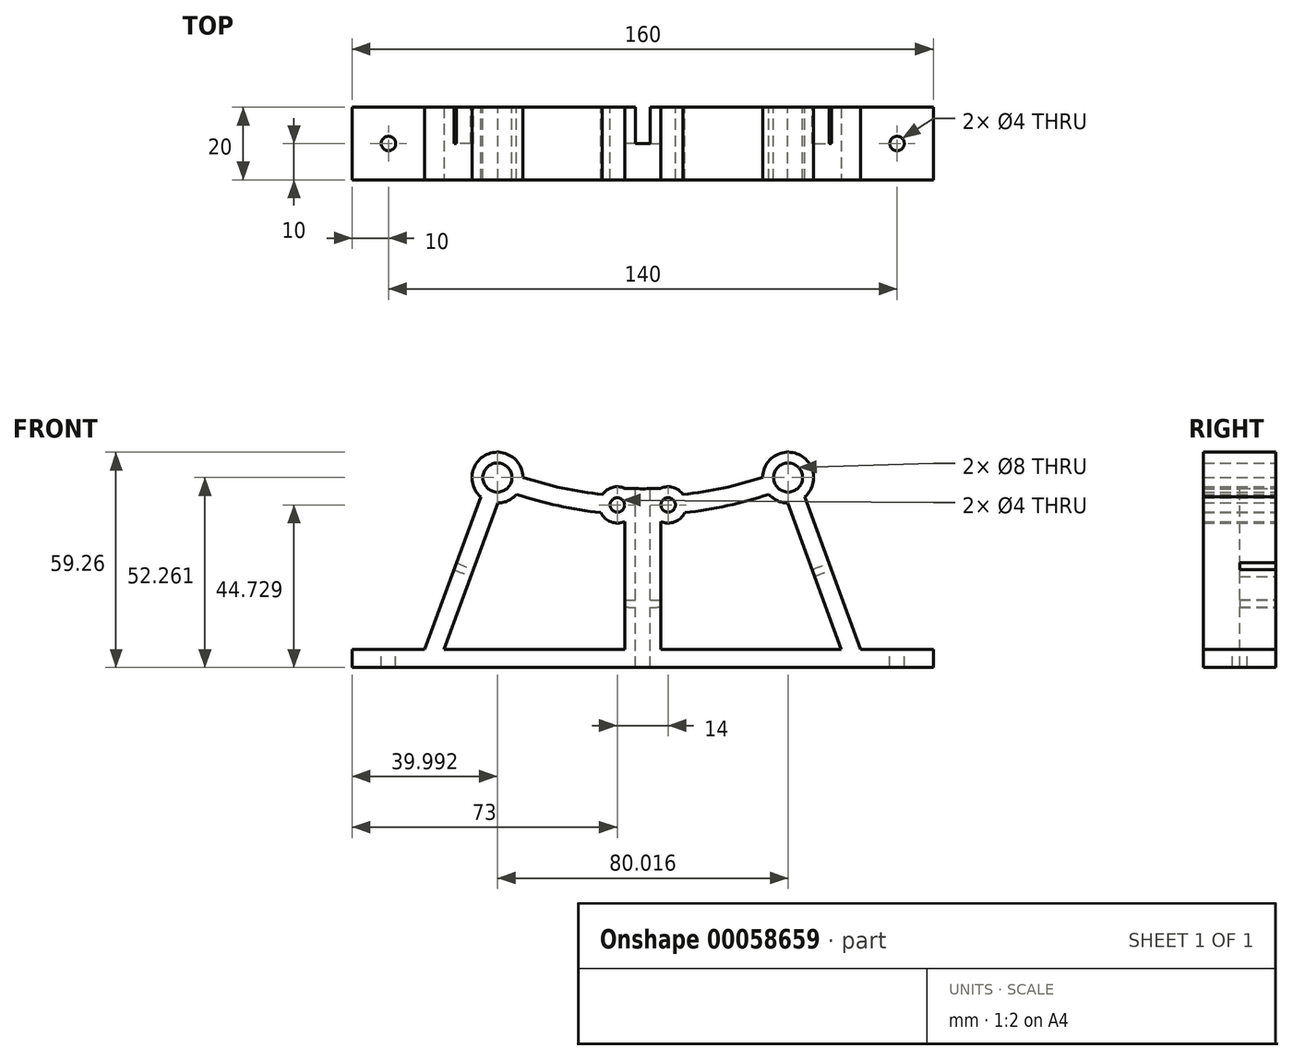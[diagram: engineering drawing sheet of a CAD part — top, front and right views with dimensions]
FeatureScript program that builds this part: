
annotation { "Feature Type Name" : "Feature", "Feature Type Description" : "" }
export const myFeature = defineFeature(function(context is Context, id is Id, definition is map)
    precondition{}
    {
        {
            var Q0;
            Q0=qCreatedBy(makeId("Front.planeOp"),FACE);
            var sketch = newSketch(context, id + "F0", { "sketchPlane" : qUnion([Q0])});
            skLineSegment(sketch, "E0", {"start": v(0, 0) * mm, "end": v(80, 0) * mm});
            skLineSegment(sketch, "E1", {"start": v(80, 0) * mm, "end": v(80, 5) * mm});
            skLineSegment(sketch, "E2", {"start": v(80, 5) * mm, "end": v(60, 5) * mm});
            skLineSegment(sketch, "E3", {"start": v(60, 5) * mm, "end": v(10.5, 140) * mm});
            skLineSegment(sketch, "E4", {"start": v(0, 0) * mm, "end": v(0, 151.5) * mm, "construction": true});
            skLineSegment(sketch, "E5.rect.bottom", {"start": v(21, 140) * mm, "end": v(0, 140) * mm, "construction": true});
            skLineSegment(sketch, "E5.rect.left", {"start": v(21, 140) * mm, "end": v(21, 163) * mm});
            skCircle(sketch, "E6", {"center": v(0, 151.5) * mm, "radius": 135 * mm, "construction": true});
            skCircle(sketch, "E7", {"center": v(0, 151.5) * mm, "radius": 133 * mm, "construction": true});
            skCircle(sketch, "E8", {"center": v(0, 151.5) * mm, "radius": 100 * mm, "construction": true});
            skLineSegment(sketch, "E9", {"start": v(21, 163) * mm, "end": v(0, 163) * mm, "construction": true});
            skLineSegment(sketch, "E10", {"start": v(0, 163) * mm, "end": v(0, 151.5) * mm, "construction": true});
            skLineSegment(sketch, "E11", {"start": v(35.25, 72.5) * mm, "end": v(0, 72.5) * mm});
            skLineSegment(sketch, "E12", {"start": v(0, 151.5) * mm, "end": v(21, 151.5) * mm, "construction": true});
            skSolve(sketch);
        }
        {
            var Q0;
            Q0=qCreatedBy(makeId("Front.planeOp"),FACE);
            var sketch = newSketch(context, id + "F1", { "sketchPlane" : qUnion([Q0])});
            skLineSegment(sketch, "E13.bottom", {"start": v(0, 0) * mm, "end": v(80, 0) * mm});
            skLineSegment(sketch, "E13.top", {"start": v(0, 5) * mm, "end": v(80, 5) * mm});
            skLineSegment(sketch, "E13.left", {"start": v(0, 0) * mm, "end": v(0, 5) * mm});
            skLineSegment(sketch, "E13.right", {"start": v(80, 0) * mm, "end": v(80, 5) * mm});
            skSolve(sketch);
        }
        {
            var Q0;
            Q0 = qSketchRegion(id + "F1", true);
            extrude(context, id + "F2", {"entities" : qUnion([Q0]), "depth" : 10 * mm});
        }
        {
            var Q0;
            Q0=qCreatedBy(makeId("Front.planeOp"),FACE);
            var sketch = newSketch(context, id + "F3", { "sketchPlane" : qUnion([Q0])});
            skLineSegment(sketch, "E14", {"start": v(0, 0) * mm, "end": v(0, 151.5) * mm});
            skLineSegment(sketch, "E15", {"start": v(0, 151.5) * mm, "end": v(5, 151.5) * mm});
            skLineSegment(sketch, "E16", {"start": v(5, 151.5) * mm, "end": v(5, 0) * mm});
            skLineSegment(sketch, "E17", {"start": v(5, 0) * mm, "end": v(0, 0) * mm});
            skSolve(sketch);
        }
        {
            var Q0;
            Q0 = qSketchRegion(id + "F3", true);
            var Q1;
            Q1=makeQuery(id+"F2.opExtrude","CAP_FACE",FACE,{"disambiguationData":[OSD([sQuery(id+"F1.wireOp",EDGE,"E13.bottom"),sQuery(id+"F1.wireOp",EDGE,"E13.top"),sQuery(id+"F1.wireOp",EDGE,"E13.left"),sQuery(id+"F1.wireOp",EDGE,"E13.right")])],"isStart":false});
            extrude(context, id + "F4", {"entities" : qUnion([Q0]), "operationType" : NewBodyOperationType.ADD, "endBound" : BoundingType.UP_TO_SURFACE, "endBoundEntityFace" : qUnion([Q1]), "depth" : 25 * mm});
        }
        {
            var Q0;
            Q0=qCreatedBy(makeId("Front.planeOp"),FACE);
            var sketch = newSketch(context, id + "F5", { "sketchPlane" : qUnion([Q0])});
            skLineSegment(sketch, "E18.bottom", {"start": v(0, 163) * mm, "end": v(21, 163) * mm});
            skLineSegment(sketch, "E18.top", {"start": v(0, 140) * mm, "end": v(21, 140) * mm});
            skLineSegment(sketch, "E18.left", {"start": v(0, 163) * mm, "end": v(0, 140) * mm});
            skLineSegment(sketch, "E18.right", {"start": v(21, 163) * mm, "end": v(21, 140) * mm});
            skSolve(sketch);
        }
        {
            var Q0;
            Q0 = qSketchRegion(id + "F5", true);
            var Q1;
            Q1=makeQuery(id+"F4.boolean.opBoolean","MERGE",FACE,{"derivedFrom":[makeQuery(id+"F2.opExtrude","CAP_FACE",FACE,{"disambiguationData":[OSD([sQuery(id+"F1.wireOp",EDGE,"E13.bottom"),sQuery(id+"F1.wireOp",EDGE,"E13.top"),sQuery(id+"F1.wireOp",EDGE,"E13.left"),sQuery(id+"F1.wireOp",EDGE,"E13.right")])],"isStart":false}),makeQuery(id+"F4.opExtrude","CAP_FACE",FACE,{"disambiguationData":[OSD([sQuery(id+"F3.wireOp",EDGE,"E14"),sQuery(id+"F3.wireOp",EDGE,"E15"),sQuery(id+"F3.wireOp",EDGE,"E16"),sQuery(id+"F3.wireOp",EDGE,"E17")])],"isStart":false})]});
            extrude(context, id + "F6", {"entities" : qUnion([Q0]), "operationType" : NewBodyOperationType.ADD, "endBound" : BoundingType.UP_TO_SURFACE, "endBoundEntityFace" : qUnion([Q1]), "depth" : 25 * mm});
        }
        {
            var Q0;
            Q0=qCreatedBy(makeId("Front.planeOp"),FACE);
            var sketch = newSketch(context, id + "F7", { "sketchPlane" : qUnion([Q0])});
            skLineSegment(sketch, "E19", {"start": v(9.87, 141.72) * mm, "end": v(60, 5) * mm});
            skLineSegment(sketch, "E20", {"start": v(60, 5) * mm, "end": v(55.3, 3.28) * mm});
            skLineSegment(sketch, "E21", {"start": v(55.3, 3.28) * mm, "end": v(5.17, 140) * mm});
            skLineSegment(sketch, "E22", {"start": v(5.17, 140) * mm, "end": v(9.87, 141.72) * mm});
            skSolve(sketch);
        }
        {
            var Q0;
            Q0 = qSketchRegion(id + "F7", true);
            var Q1;
            Q1=makeQuery(id+"F6.boolean.opBoolean","MERGE",FACE,{"derivedFrom":[makeQuery(id+"F4.boolean.opBoolean","MERGE",FACE,{"derivedFrom":[makeQuery(id+"F2.opExtrude","CAP_FACE",FACE,{"disambiguationData":[OSD([sQuery(id+"F1.wireOp",EDGE,"E13.bottom"),sQuery(id+"F1.wireOp",EDGE,"E13.top"),sQuery(id+"F1.wireOp",EDGE,"E13.left"),sQuery(id+"F1.wireOp",EDGE,"E13.right")])],"isStart":false}),makeQuery(id+"F4.opExtrude","CAP_FACE",FACE,{"disambiguationData":[OSD([sQuery(id+"F3.wireOp",EDGE,"E14"),sQuery(id+"F3.wireOp",EDGE,"E15"),sQuery(id+"F3.wireOp",EDGE,"E16"),sQuery(id+"F3.wireOp",EDGE,"E17")])],"isStart":false})]}),makeQuery(id+"F6.opExtrude","CAP_FACE",FACE,{"disambiguationData":[OSD([sQuery(id+"F5.wireOp",EDGE,"E18.bottom"),sQuery(id+"F5.wireOp",EDGE,"E18.top"),sQuery(id+"F5.wireOp",EDGE,"E18.left"),sQuery(id+"F5.wireOp",EDGE,"E18.right")])],"isStart":false})]});
            extrude(context, id + "F8", {"entities" : qUnion([Q0]), "operationType" : NewBodyOperationType.ADD, "endBound" : BoundingType.UP_TO_SURFACE, "endBoundEntityFace" : qUnion([Q1]), "depth" : 25 * mm});
        }
        {
            var Q0;
            Q0=makeQuery(id+"F8.boolean.opBoolean","MERGE",FACE,{"derivedFrom":[makeQuery(id+"F6.boolean.opBoolean","MERGE",FACE,{"derivedFrom":[makeQuery(id+"F4.boolean.opBoolean","MERGE",FACE,{"derivedFrom":[makeQuery(id+"F2.opExtrude","CAP_FACE",FACE,{"disambiguationData":[OSD([sQuery(id+"F1.wireOp",EDGE,"E13.bottom"),sQuery(id+"F1.wireOp",EDGE,"E13.top"),sQuery(id+"F1.wireOp",EDGE,"E13.left"),sQuery(id+"F1.wireOp",EDGE,"E13.right")])],"isStart":false}),makeQuery(id+"F4.opExtrude","CAP_FACE",FACE,{"disambiguationData":[OSD([sQuery(id+"F3.wireOp",EDGE,"E14"),sQuery(id+"F3.wireOp",EDGE,"E15"),sQuery(id+"F3.wireOp",EDGE,"E16"),sQuery(id+"F3.wireOp",EDGE,"E17")])],"isStart":false})]}),makeQuery(id+"F6.opExtrude","CAP_FACE",FACE,{"disambiguationData":[OSD([sQuery(id+"F5.wireOp",EDGE,"E18.bottom"),sQuery(id+"F5.wireOp",EDGE,"E18.top"),sQuery(id+"F5.wireOp",EDGE,"E18.left"),sQuery(id+"F5.wireOp",EDGE,"E18.right")])],"isStart":false})]}),makeQuery(id+"F8.opExtrude","CAP_FACE",FACE,{"disambiguationData":[OSD([sQuery(id+"F7.wireOp",EDGE,"E19"),sQuery(id+"F7.wireOp",EDGE,"E20"),sQuery(id+"F7.wireOp",EDGE,"E21"),sQuery(id+"F7.wireOp",EDGE,"E22")])],"isStart":false})]});
            var sketch = newSketch(context, id + "F9", { "sketchPlane" : qUnion([Q0])});
            skLineSegment(sketch, "E23.0", {"start": v(54.67, 5) * mm, "end": v(5.17, 140) * mm});
            skLineSegment(sketch, "E24.0", {"start": v(5, 140) * mm, "end": v(5, 5) * mm});
            skLineSegment(sketch, "E25.0", {"start": v(5, 5) * mm, "end": v(54.67, 5) * mm});
            skLineSegment(sketch, "E26.0", {"start": v(0, 0) * mm, "end": v(0, 163) * mm});
            skLineSegment(sketch, "E27.0", {"start": v(0, 0) * mm, "end": v(80, 0) * mm});
            skLineSegment(sketch, "E28.0", {"start": v(60, 5) * mm, "end": v(80, 5) * mm});
            skLineSegment(sketch, "E28.1", {"start": v(80, 0) * mm, "end": v(80, 5) * mm});
            skLineSegment(sketch, "E28.2", {"start": v(10.5, 140) * mm, "end": v(60, 5) * mm});
            skLineSegment(sketch, "E29.0", {"start": v(10.5, 140) * mm, "end": v(21, 140) * mm});
            skLineSegment(sketch, "E29.1", {"start": v(21, 163) * mm, "end": v(21, 140) * mm});
            skLineSegment(sketch, "E29.2", {"start": v(0, 163) * mm, "end": v(21, 163) * mm});
            skSolve(sketch);
        }
        {
            var Q0;
            Q0=makeQuery(id+"F9.imprint","IMPRINT",FACE,{"disambiguationData":[TD([[makeQuery(id+"F9.imprint","IMPRINT",EDGE,{"derivedFrom":sQuery(id+"F9.wireOp",EDGE,"E23.0")}),-1.0]])]});
            extrude(context, id + "F10", {"entities" : qUnion([Q0]), "operationType" : NewBodyOperationType.ADD, "depth" : 10 * mm});
        }
        {
            var Q0;
            Q0=makeQuery(id+"F8.boolean.opBoolean","MERGE",FACE,{"derivedFrom":[makeQuery(id+"F6.boolean.opBoolean","MERGE",FACE,{"derivedFrom":[makeQuery(id+"F4.boolean.opBoolean","MERGE",FACE,{"derivedFrom":[makeQuery(id+"F2.opExtrude","CAP_FACE",FACE,{"disambiguationData":[OSD([sQuery(id+"F1.wireOp",EDGE,"E13.bottom"),sQuery(id+"F1.wireOp",EDGE,"E13.top"),sQuery(id+"F1.wireOp",EDGE,"E13.left"),sQuery(id+"F1.wireOp",EDGE,"E13.right")])],"isStart":true}),makeQuery(id+"F4.opExtrude","CAP_FACE",FACE,{"disambiguationData":[OSD([sQuery(id+"F3.wireOp",EDGE,"E14"),sQuery(id+"F3.wireOp",EDGE,"E15"),sQuery(id+"F3.wireOp",EDGE,"E16"),sQuery(id+"F3.wireOp",EDGE,"E17")])],"isStart":true})]}),makeQuery(id+"F6.opExtrude","CAP_FACE",FACE,{"disambiguationData":[OSD([sQuery(id+"F5.wireOp",EDGE,"E18.bottom"),sQuery(id+"F5.wireOp",EDGE,"E18.top"),sQuery(id+"F5.wireOp",EDGE,"E18.left"),sQuery(id+"F5.wireOp",EDGE,"E18.right")])],"isStart":true})]}),makeQuery(id+"F8.opExtrude","CAP_FACE",FACE,{"disambiguationData":[OSD([sQuery(id+"F7.wireOp",EDGE,"E19"),sQuery(id+"F7.wireOp",EDGE,"E20"),sQuery(id+"F7.wireOp",EDGE,"E21"),sQuery(id+"F7.wireOp",EDGE,"E22")])],"isStart":true})]});
            var sketch = newSketch(context, id + "F11", { "sketchPlane" : qUnion([Q0])});
            skLineSegment(sketch, "E30", {"start": v(0, 0) * mm, "end": v(-2, 0) * mm});
            skLineSegment(sketch, "E31", {"start": v(-2, 0) * mm, "end": v(-2, 138) * mm});
            skLineSegment(sketch, "E32", {"start": v(-2, 138) * mm, "end": v(-21, 138) * mm});
            skLineSegment(sketch, "E33", {"start": v(-21, 138) * mm, "end": v(-21, 140) * mm});
            skLineSegment(sketch, "E34", {"start": v(-21, 140) * mm, "end": v(0, 140) * mm});
            skLineSegment(sketch, "E35", {"start": v(0, 140) * mm, "end": v(0, 0) * mm});
            skSolve(sketch);
        }
        {
            var Q0;
            Q0 = qSketchRegion(id + "F11", true);
            extrude(context, id + "F12", {"entities" : qUnion([Q0]), "operationType" : NewBodyOperationType.REMOVE, "oppositeDirection" : true, "depth" : 10 * mm});
        }
        {
            var Q0;
            {var subQ0=sQuery(id+"F7.wireOp",EDGE,"E21");var subQ1=sQuery(id+"F7.wireOp",EDGE,"E19");var subQ2=sQuery(id+"F1.wireOp",EDGE,"E13.bottom");var subQ3=sQuery(id+"F1.wireOp",EDGE,"E13.top");var subQ4=sQuery(id+"F1.wireOp",EDGE,"E13.right");var subQ5=sQuery(id+"F3.wireOp",EDGE,"E16");Q0=makeQuery(id+"F12.boolean.opBoolean","SPLIT",FACE,{"disambiguationData":[TD([makeQuery(id+"F2.opExtrude","SWEPT_FACE",FACE,{"disambiguationData":[OSD([subQ2])]})])],"derivedFrom":makeQuery(id+"F8.boolean.opBoolean","MERGE",FACE,{"derivedFrom":[makeQuery(id+"F6.boolean.opBoolean","MERGE",FACE,{"derivedFrom":[makeQuery(id+"F4.boolean.opBoolean","MERGE",FACE,{"derivedFrom":[makeQuery(id+"F2.opExtrude","CAP_FACE",FACE,{"disambiguationData":[OSD([subQ2,subQ3,sQuery(id+"F1.wireOp",EDGE,"E13.left"),subQ4])],"isStart":true}),makeQuery(id+"F4.opExtrude","CAP_FACE",FACE,{"disambiguationData":[OSD([sQuery(id+"F3.wireOp",EDGE,"E14"),sQuery(id+"F3.wireOp",EDGE,"E15"),subQ5,sQuery(id+"F3.wireOp",EDGE,"E17")])],"isStart":true})]}),makeQuery(id+"F6.opExtrude","CAP_FACE",FACE,{"disambiguationData":[OSD([sQuery(id+"F5.wireOp",EDGE,"E18.bottom"),sQuery(id+"F5.wireOp",EDGE,"E18.top"),sQuery(id+"F5.wireOp",EDGE,"E18.left"),sQuery(id+"F5.wireOp",EDGE,"E18.right")])],"isStart":true})]}),makeQuery(id+"F8.opExtrude","CAP_FACE",FACE,{"disambiguationData":[OSD([subQ1,sQuery(id+"F7.wireOp",EDGE,"E20"),subQ0,sQuery(id+"F7.wireOp",EDGE,"E22")])],"isStart":true})]})});}
            var sketch = newSketch(context, id + "F13", { "sketchPlane" : qUnion([Q0])});
            skLineSegment(sketch, "E36", {"start": v(-2, 138) * mm, "end": v(-11.23, 138) * mm});
            skLineSegment(sketch, "E37", {"start": v(-11.23, 138) * mm, "end": v(-13.07, 133) * mm});
            skLineSegment(sketch, "E38", {"start": v(-13.07, 133) * mm, "end": v(-2, 133) * mm});
            skLineSegment(sketch, "E39", {"start": v(-2, 133) * mm, "end": v(-2, 138) * mm});
            skSolve(sketch);
        }
        {
            var Q0;
            Q0 = qSketchRegion(id + "F13", true);
            extrude(context, id + "F14", {"entities" : qUnion([Q0]), "operationType" : NewBodyOperationType.ADD, "oppositeDirection" : true, "depth" : 20 * mm});
        }
        {
            var Q0;
            Q0=makeQuery(id+"F14.boolean.opBoolean","MERGE",FACE,{"derivedFrom":[makeQuery(id+"F10.opExtrude","CAP_FACE",FACE,{"disambiguationData":[OSD([sQuery(id+"F5.wireOp",EDGE,"E18.top"),sQuery(id+"F9.wireOp",EDGE,"E23.0"),sQuery(id+"F9.wireOp",EDGE,"E24.0"),sQuery(id+"F9.wireOp",EDGE,"E25.0"),sQuery(id+"F9.wireOp",EDGE,"E26.0"),sQuery(id+"F9.wireOp",EDGE,"E27.0"),sQuery(id+"F9.wireOp",EDGE,"E28.0"),sQuery(id+"F9.wireOp",EDGE,"E28.1"),sQuery(id+"F9.wireOp",EDGE,"E28.2"),sQuery(id+"F9.wireOp",EDGE,"E29.0"),sQuery(id+"F9.wireOp",EDGE,"E29.1"),sQuery(id+"F9.wireOp",EDGE,"E29.2")])],"isStart":false}),makeQuery(id+"F14.opExtrude","CAP_FACE",FACE,{"disambiguationData":[OSD([sQuery(id+"F13.wireOp",EDGE,"E36"),sQuery(id+"F13.wireOp",EDGE,"E37"),sQuery(id+"F13.wireOp",EDGE,"E38"),sQuery(id+"F13.wireOp",EDGE,"E39")])],"isStart":false})]});
            var sketch = newSketch(context, id + "F15", { "sketchPlane" : qUnion([Q0])});
            skLineSegment(sketch, "E40.bottom", {"start": v(5, 140) * mm, "end": v(5.9, 140) * mm});
            skLineSegment(sketch, "E40.top", {"start": v(5, 138) * mm, "end": v(5.9, 138) * mm});
            skLineSegment(sketch, "E40.left", {"start": v(5, 140) * mm, "end": v(5, 138) * mm});
            skLineSegment(sketch, "E40.right", {"start": v(5.9, 140) * mm, "end": v(5.9, 138) * mm});
            skSolve(sketch);
        }
        {
            var Q0;
            Q0 = qSketchRegion(id + "F15", true);
            extrude(context, id + "F16", {"entities" : qUnion([Q0]), "operationType" : NewBodyOperationType.ADD, "oppositeDirection" : true, "depth" : 10 * mm});
        }
        {
            var Q0;
            Q0=qCreatedBy(makeId("Front.planeOp"),FACE);
            var sketch = newSketch(context, id + "F17", { "sketchPlane" : qUnion([Q0])});
            skCircle(sketch, "E41.0", {"center": v(0, 151.5) * mm, "radius": 135 * mm});
            skCircle(sketch, "E41.1", {"center": v(0, 151.5) * mm, "radius": 133 * mm});
            skSolve(sketch);
        }
        {
            var Q0;
            Q0 = qSketchRegion(id + "F17", true);
            extrude(context, id + "F18", {"entities" : qUnion([Q0]), "operationType" : NewBodyOperationType.REMOVE, "depth" : 10 * mm});
        }
        {
            var Q0;
            Q0=qCreatedBy(makeId("Front.planeOp"),FACE);
            var sketch = newSketch(context, id + "F19", { "sketchPlane" : qUnion([Q0])});
            skCircle(sketch, "E42", {"center": v(40, 52.26) * mm, "radius": 7 * mm});
            skCircle(sketch, "E43", {"center": v(40, 52.26) * mm, "radius": 4 * mm});
            skPoint(sketch, "E44", {"position": v(42.36, 53.12) * mm});
            skPoint(sketch, "E45", {"position": v(37.66, 51.4) * mm});
            skLineSegment(sketch, "E46", {"start": v(37.66, 51.4) * mm, "end": v(42.36, 53.12) * mm, "construction": true});
            skSolve(sketch);
        }
        {
            var Q0;
            Q0 = qSketchRegion(id + "F19", true);
            var Q1;
            Q1=makeQuery(id+"F16.boolean.opBoolean","MERGE",FACE,{"derivedFrom":[makeQuery(id+"F14.boolean.opBoolean","MERGE",FACE,{"derivedFrom":[makeQuery(id+"F10.opExtrude","CAP_FACE",FACE,{"disambiguationData":[OSD([sQuery(id+"F5.wireOp",EDGE,"E18.top"),sQuery(id+"F9.wireOp",EDGE,"E23.0"),sQuery(id+"F9.wireOp",EDGE,"E24.0"),sQuery(id+"F9.wireOp",EDGE,"E25.0"),sQuery(id+"F9.wireOp",EDGE,"E26.0"),sQuery(id+"F9.wireOp",EDGE,"E27.0"),sQuery(id+"F9.wireOp",EDGE,"E28.0"),sQuery(id+"F9.wireOp",EDGE,"E28.1"),sQuery(id+"F9.wireOp",EDGE,"E28.2"),sQuery(id+"F9.wireOp",EDGE,"E29.0"),sQuery(id+"F9.wireOp",EDGE,"E29.1"),sQuery(id+"F9.wireOp",EDGE,"E29.2")])],"isStart":false}),makeQuery(id+"F14.opExtrude","CAP_FACE",FACE,{"disambiguationData":[OSD([sQuery(id+"F13.wireOp",EDGE,"E36"),sQuery(id+"F13.wireOp",EDGE,"E37"),sQuery(id+"F13.wireOp",EDGE,"E38"),sQuery(id+"F13.wireOp",EDGE,"E39")])],"isStart":false})]}),makeQuery(id+"F16.opExtrude","CAP_FACE",FACE,{"disambiguationData":[OSD([sQuery(id+"F15.wireOp",EDGE,"E40.bottom"),sQuery(id+"F15.wireOp",EDGE,"E40.top"),sQuery(id+"F15.wireOp",EDGE,"E40.left"),sQuery(id+"F15.wireOp",EDGE,"E40.right")])],"isStart":true})]});
            extrude(context, id + "F20", {"entities" : qUnion([Q0]), "operationType" : NewBodyOperationType.ADD, "endBound" : BoundingType.UP_TO_SURFACE, "endBoundEntityFace" : qUnion([Q1]), "depth" : 25 * mm});
        }
        {
            var Q0;
            Q0=qCreatedBy(makeId("Front.planeOp"),FACE);
            var sketch = newSketch(context, id + "F21", { "sketchPlane" : qUnion([Q0])});
            skCircle(sketch, "E47", {"center": v(40, 52.26) * mm, "radius": 4 * mm});
            skSolve(sketch);
        }
        {
            var Q0;
            Q0 = qSketchRegion(id + "F21", true);
            extrude(context, id + "F22", {"entities" : qUnion([Q0]), "operationType" : NewBodyOperationType.REMOVE, "endBound" : BoundingType.THROUGH_ALL, "depth" : 25 * mm});
        }
        {
            var Q0;
            Q0=qCreatedBy(makeId("Front.planeOp"),FACE);
            var sketch = newSketch(context, id + "F23", { "sketchPlane" : qUnion([Q0])});
            skCircle(sketch, "E48", {"center": v(7, 44.73) * mm, "radius": 5 * mm});
            skCircle(sketch, "E49", {"center": v(7, 44.73) * mm, "radius": 2 * mm});
            skCircle(sketch, "E50", {"center": v(0, 151.5) * mm, "radius": 107 * mm, "construction": true});
            skSolve(sketch);
        }
        {
            var Q0;
            Q0 = qSketchRegion(id + "F23", true);
            var Q1;
            Q1=makeQuery(id+"F20.boolean.opBoolean","MERGE",FACE,{"derivedFrom":[makeQuery(id+"F16.boolean.opBoolean","MERGE",FACE,{"derivedFrom":[makeQuery(id+"F14.boolean.opBoolean","MERGE",FACE,{"derivedFrom":[makeQuery(id+"F10.opExtrude","CAP_FACE",FACE,{"disambiguationData":[OSD([sQuery(id+"F5.wireOp",EDGE,"E18.top"),sQuery(id+"F9.wireOp",EDGE,"E23.0"),sQuery(id+"F9.wireOp",EDGE,"E24.0"),sQuery(id+"F9.wireOp",EDGE,"E25.0"),sQuery(id+"F9.wireOp",EDGE,"E26.0"),sQuery(id+"F9.wireOp",EDGE,"E27.0"),sQuery(id+"F9.wireOp",EDGE,"E28.0"),sQuery(id+"F9.wireOp",EDGE,"E28.1"),sQuery(id+"F9.wireOp",EDGE,"E28.2"),sQuery(id+"F9.wireOp",EDGE,"E29.0"),sQuery(id+"F9.wireOp",EDGE,"E29.1"),sQuery(id+"F9.wireOp",EDGE,"E29.2")])],"isStart":false}),makeQuery(id+"F14.opExtrude","CAP_FACE",FACE,{"disambiguationData":[OSD([sQuery(id+"F13.wireOp",EDGE,"E36"),sQuery(id+"F13.wireOp",EDGE,"E37"),sQuery(id+"F13.wireOp",EDGE,"E38"),sQuery(id+"F13.wireOp",EDGE,"E39")])],"isStart":false})]}),makeQuery(id+"F16.opExtrude","CAP_FACE",FACE,{"disambiguationData":[OSD([sQuery(id+"F15.wireOp",EDGE,"E40.bottom"),sQuery(id+"F15.wireOp",EDGE,"E40.top"),sQuery(id+"F15.wireOp",EDGE,"E40.left"),sQuery(id+"F15.wireOp",EDGE,"E40.right")])],"isStart":true})]}),makeQuery(id+"F20.opExtrude","CAP_FACE",FACE,{"disambiguationData":[OSD([sQuery(id+"F19.wireOp",EDGE,"E42"),sQuery(id+"F19.wireOp",EDGE,"E43")])],"isStart":false})]});
            extrude(context, id + "F24", {"entities" : qUnion([Q0]), "operationType" : NewBodyOperationType.ADD, "endBound" : BoundingType.UP_TO_SURFACE, "endBoundEntityFace" : qUnion([Q1]), "depth" : 25 * mm});
        }
        {
            var Q0;
            Q0=qCreatedBy(makeId("Front.planeOp"),FACE);
            var sketch = newSketch(context, id + "F25", { "sketchPlane" : qUnion([Q0])});
            skCircle(sketch, "E51", {"center": v(0, 151.5) * mm, "radius": 107 * mm, "construction": true});
            skArc(sketch, "E52", {"start": v(9, 44.88) * mm, "mid": v(22.83, 46.96) * mm, "end": v(36.27, 50.84) * mm});
            skArc(sketch, "E53.0.left", {"start": v(8.78, 47.37) * mm, "mid": v(22.3, 49.4) * mm, "end": v(35.42, 53.19) * mm});
            skArc(sketch, "E53.0.right", {"start": v(9.2, 42.39) * mm, "mid": v(23.36, 44.52) * mm, "end": v(37.12, 48.48) * mm});
            skLineSegment(sketch, "E54", {"start": v(35.42, 53.19) * mm, "end": v(37.12, 48.48) * mm});
            skLineSegment(sketch, "E55", {"start": v(8.78, 47.37) * mm, "end": v(9.2, 42.39) * mm});
            skSolve(sketch);
        }
        {
            var Q0;
            Q0 = qSketchRegion(id + "F25", true);
            var Q1;
            Q1=makeQuery(id+"F24.boolean.opBoolean","MERGE",FACE,{"derivedFrom":[makeQuery(id+"F20.boolean.opBoolean","MERGE",FACE,{"derivedFrom":[makeQuery(id+"F16.boolean.opBoolean","MERGE",FACE,{"derivedFrom":[makeQuery(id+"F14.boolean.opBoolean","MERGE",FACE,{"derivedFrom":[makeQuery(id+"F10.opExtrude","CAP_FACE",FACE,{"disambiguationData":[OSD([sQuery(id+"F5.wireOp",EDGE,"E18.top"),sQuery(id+"F9.wireOp",EDGE,"E23.0"),sQuery(id+"F9.wireOp",EDGE,"E24.0"),sQuery(id+"F9.wireOp",EDGE,"E25.0"),sQuery(id+"F9.wireOp",EDGE,"E26.0"),sQuery(id+"F9.wireOp",EDGE,"E27.0"),sQuery(id+"F9.wireOp",EDGE,"E28.0"),sQuery(id+"F9.wireOp",EDGE,"E28.1"),sQuery(id+"F9.wireOp",EDGE,"E28.2"),sQuery(id+"F9.wireOp",EDGE,"E29.0"),sQuery(id+"F9.wireOp",EDGE,"E29.1"),sQuery(id+"F9.wireOp",EDGE,"E29.2")])],"isStart":false}),makeQuery(id+"F14.opExtrude","CAP_FACE",FACE,{"disambiguationData":[OSD([sQuery(id+"F13.wireOp",EDGE,"E36"),sQuery(id+"F13.wireOp",EDGE,"E37"),sQuery(id+"F13.wireOp",EDGE,"E38"),sQuery(id+"F13.wireOp",EDGE,"E39")])],"isStart":false})]}),makeQuery(id+"F16.opExtrude","CAP_FACE",FACE,{"disambiguationData":[OSD([sQuery(id+"F15.wireOp",EDGE,"E40.bottom"),sQuery(id+"F15.wireOp",EDGE,"E40.top"),sQuery(id+"F15.wireOp",EDGE,"E40.left"),sQuery(id+"F15.wireOp",EDGE,"E40.right")])],"isStart":true})]}),makeQuery(id+"F20.opExtrude","CAP_FACE",FACE,{"disambiguationData":[OSD([sQuery(id+"F19.wireOp",EDGE,"E42"),sQuery(id+"F19.wireOp",EDGE,"E43")])],"isStart":false})]}),makeQuery(id+"F24.opExtrude","CAP_FACE",FACE,{"disambiguationData":[OSD([sQuery(id+"F23.wireOp",EDGE,"E48"),sQuery(id+"F23.wireOp",EDGE,"E49")])],"isStart":false})]});
            extrude(context, id + "F26", {"entities" : qUnion([Q0]), "operationType" : NewBodyOperationType.ADD, "endBound" : BoundingType.UP_TO_SURFACE, "endBoundEntityFace" : qUnion([Q1]), "depth" : 25 * mm});
        }
        {
            var Q0;
            Q0=qCreatedBy(makeId("Front.planeOp"),FACE);
            var sketch = newSketch(context, id + "F27", { "sketchPlane" : qUnion([Q0])});
            skArc(sketch, "E56.0", {"start": v(11.1, 47.6) * mm, "mid": v(22.18, 49.38) * mm, "end": v(33, 52.35) * mm});
            skArc(sketch, "E56.1", {"start": v(11.1, 47.6) * mm, "mid": v(8.36, 49.54) * mm, "end": v(5, 49.31) * mm});
            skArc(sketch, "E56.2", {"start": v(46.41, 55.09) * mm, "mid": v(38.6, 59.12) * mm, "end": v(33, 52.35) * mm});
            skArc(sketch, "E57", {"start": v(0, 253.81) * mm, "mid": v(-102.28, 149) * mm, "end": v(5, 49.31) * mm});
            skArc(sketch, "E58", {"start": v(46.41, 55.09) * mm, "mid": v(104.32, 175.3) * mm, "end": v(0, 258.5) * mm});
            skLineSegment(sketch, "E59", {"start": v(0, 258.5) * mm, "end": v(0, 253.81) * mm});
            skSolve(sketch);
        }
        {
            var Q0;
            Q0 = qSketchRegion(id + "F27", true);
            extrude(context, id + "F28", {"entities" : qUnion([Q0]), "operationType" : NewBodyOperationType.REMOVE, "endBound" : BoundingType.THROUGH_ALL, "depth" : 25 * mm});
        }
        {
            var Q0;
            {var subQ4=sQuery(id+"F1.wireOp",EDGE,"E13.right");var subQ6=sQuery(id+"F1.wireOp",EDGE,"E13.top");Q0=makeQuery(id+"F10.boolean.opBoolean","MERGE",FACE,{"derivedFrom":[makeQuery(id+"F8.boolean.opBoolean","SPLIT",FACE,{"disambiguationData":[TD([makeQuery(id+"F2.opExtrude","SWEPT_FACE",FACE,{"disambiguationData":[OSD([subQ4])]})])],"derivedFrom":makeQuery(id+"F2.opExtrude","SWEPT_FACE",FACE,{"disambiguationData":[OSD([subQ6])]})}),makeQuery(id+"F10.opExtrude","SWEPT_FACE",FACE,{"disambiguationData":[OSD([sQuery(id+"F9.wireOp",EDGE,"E28.0")])]})]});}
            var sketch = newSketch(context, id + "F29", { "sketchPlane" : qUnion([Q0])});
            skLineSegment(sketch, "E60", {"start": v(60, 0) * mm, "end": v(80, -20) * mm, "construction": true});
            skCircle(sketch, "E61", {"center": v(70, -10) * mm, "radius": 2 * mm});
            skSolve(sketch);
        }
        {
            var Q0;
            Q0 = qSketchRegion(id + "F29", true);
            extrude(context, id + "F30", {"entities" : qUnion([Q0]), "operationType" : NewBodyOperationType.REMOVE, "endBound" : BoundingType.THROUGH_ALL, "oppositeDirection" : true, "depth" : 25 * mm});
        }
        {
            var Q0;
            Q0=makeQuery(id+"F2.opExtrude","SWEPT_BODY",BODY,{"disambiguationData":[OSD([sQuery(id+"F1.wireOp",EDGE,"E13.bottom"),sQuery(id+"F1.wireOp",EDGE,"E13.top"),sQuery(id+"F1.wireOp",EDGE,"E13.left"),sQuery(id+"F1.wireOp",EDGE,"E13.right")])]});
            var Q1;
            Q1=qCreatedBy(makeId("Right.planeOp"),FACE);
            mirror(context, id + "F31", {"operationType" : NewBodyOperationType.ADD, "entities" : qUnion([Q0]), "mirrorPlane" : qUnion([Q1])});
        }
    });
